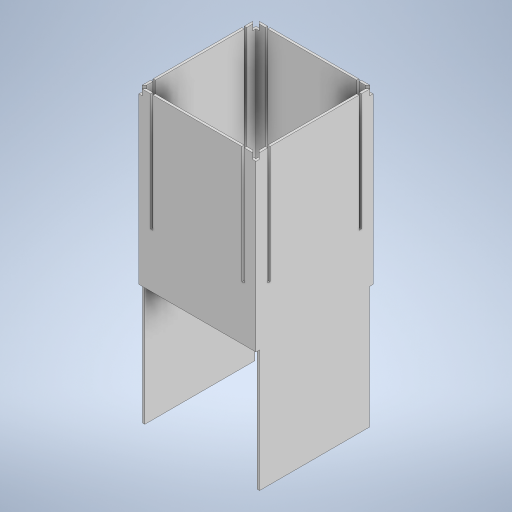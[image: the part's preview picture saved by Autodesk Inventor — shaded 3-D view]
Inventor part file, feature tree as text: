
AUTODESK INVENTOR PART (.ipt)
format: ipt  version: 2024.3 (Build 283343000, 343)  size: 316,416 bytes
history: native  units: mm
features: extrude x6, sketch x6, mirror x3, plane x2
ambient origin geometry x8: Origin, YZ Plane, XZ Plane, XY Plane, X Axis, Y Axis, Z Axis, Center Point
bodies: Solid1 (feature_tree)
feature tree (17):
  extrude  "Extrusion1"  Depth=100.0mm
  extrude  "Extrusion2"  Depth=250.0mm TaperAngle=0.0deg
  mirror  "Mirror1"
  extrude  "Extrusion3"  Depth=104.0mm
  mirror  "Mirror2"
  extrude  "Extrusion4"  Depth=100.0mm
  mirror  "Mirror3"
  plane  "Work Plane1"
  sketch  "Sketch5"  dims[d10=2.0mm d11=10.0mm]
  extrude  "Extrusion5"  Depth=10.0mm
  plane  "Work Plane2"
  extrude  "Extrusion6"  Depth=10.0mm
  sketch  "Sketch1"  dims[d0=100.0mm d1=100.0mm]
  sketch  "Sketch2"  dims[d2=2.0mm d3=250.0mm d4=0.0mm]
  sketch  "Sketch3"  dims[d5=3.0mm d6=104.0mm]
  sketch  "Sketch4"  dims[d7=220.0mm d8=0.0mm d9=100.0mm]
  sketch  "Sketch6"  dims[d12=220.0mm d13=0.0mm d14=10.0mm d15=2.0mm d16=100.0mm d17=0.0mm d18=220.0mm d19=0.0mm d20=5.0mm d21=4.0mm d22=0.0mm d23=0.0mm d24=220.0mm d25=0.0mm d26=4.0mm d27=5.0mm d28=0.0mm d29=220.0mm d30=0.0mm]
